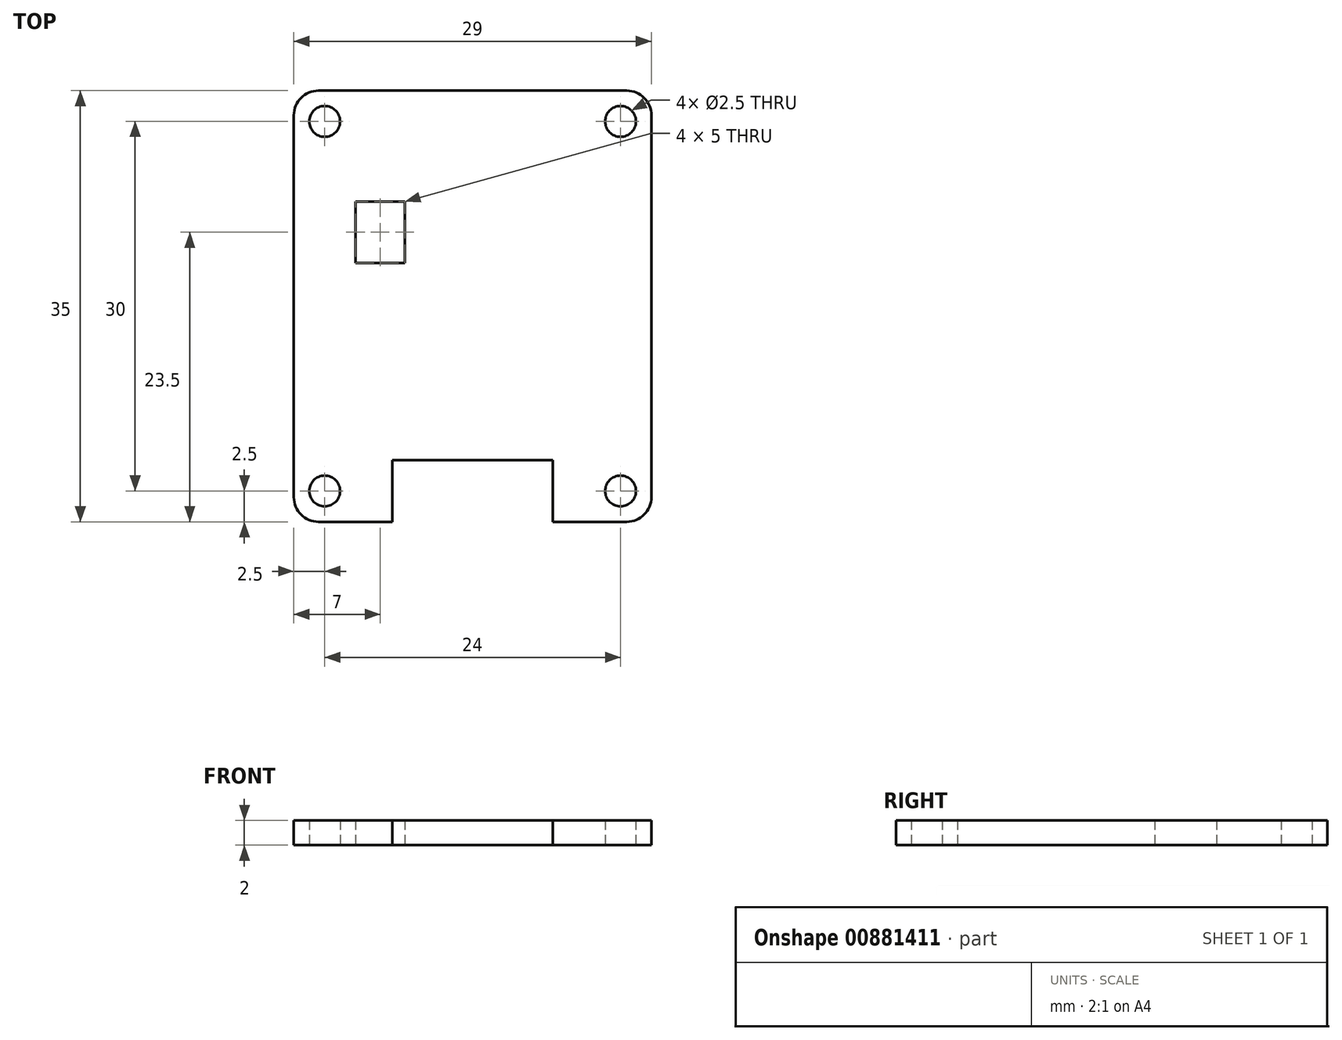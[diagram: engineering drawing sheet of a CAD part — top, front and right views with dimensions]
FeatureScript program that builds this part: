
annotation { "Feature Type Name" : "Feature", "Feature Type Description" : "" }
export const myFeature = defineFeature(function(context is Context, id is Id, definition is map)
    precondition{}
    {
        {
            var Q0;
            Q0=qCreatedBy(makeId("Top.planeOp"),FACE);
            var sketch = newSketch(context, id + "F0", { "sketchPlane" : qUnion([Q0])});
            skLineSegment(sketch, "E0.bottom", {"start": v(9.5, -12.5) * mm, "end": v(-9.5, -12.5) * mm});
            skLineSegment(sketch, "E0.top", {"start": v(9.5, 12.5) * mm, "end": v(-9.5, 12.5) * mm});
            skLineSegment(sketch, "E0.left", {"start": v(9.5, -12.5) * mm, "end": v(9.5, 12.5) * mm});
            skLineSegment(sketch, "E0.right", {"start": v(-9.5, -12.5) * mm, "end": v(-9.5, 12.5) * mm});
            skPoint(sketch, "E0.middle", {"position": v(0, 0) * mm});
            skLineSegment(sketch, "E1.0", {"start": v(14.5, 17.5) * mm, "end": v(-14.5, 17.5) * mm});
            skLineSegment(sketch, "E1.1", {"start": v(14.5, -17.5) * mm, "end": v(14.5, 17.5) * mm});
            skLineSegment(sketch, "E1.2", {"start": v(14.5, -17.5) * mm, "end": v(-14.5, -17.5) * mm});
            skLineSegment(sketch, "E1.3", {"start": v(-14.5, -17.5) * mm, "end": v(-14.5, 17.5) * mm});
            skPoint(sketch, "E2", {"position": v(12, 15) * mm});
            skPoint(sketch, "E3", {"position": v(-12, 15) * mm});
            skPoint(sketch, "E4", {"position": v(-12, -15) * mm});
            skPoint(sketch, "E5", {"position": v(12, -15) * mm});
            skCircle(sketch, "E6", {"center": v(-12, -15) * mm, "radius": 1.25 * mm});
            skCircle(sketch, "E7", {"center": v(12, -15) * mm, "radius": 1.25 * mm});
            skCircle(sketch, "E8", {"center": v(12, 15) * mm, "radius": 1.25 * mm});
            skCircle(sketch, "E9", {"center": v(-12, 15) * mm, "radius": 1.25 * mm});
            skPoint(sketch, "E10", {"position": v(-9.5, 8.5) * mm});
            skPoint(sketch, "E11", {"position": v(-5.5, 8.5) * mm});
            skPoint(sketch, "E12", {"position": v(-5.5, 3.5) * mm});
            skPoint(sketch, "E13", {"position": v(-9.5, 3.5) * mm});
            skLineSegment(sketch, "E14", {"start": v(-9.5, 8.5) * mm, "end": v(-5.5, 8.5) * mm});
            skLineSegment(sketch, "E15", {"start": v(-5.5, 8.5) * mm, "end": v(-5.5, 3.5) * mm});
            skLineSegment(sketch, "E16", {"start": v(-5.5, 3.5) * mm, "end": v(-9.5, 3.5) * mm});
            skPoint(sketch, "E17", {"position": v(6.5, -12.5) * mm});
            skPoint(sketch, "E18", {"position": v(-6.5, -12.5) * mm});
            skLineSegment(sketch, "E19", {"start": v(-6.5, -12.5) * mm, "end": v(-6.5, -17.5) * mm});
            skLineSegment(sketch, "E20", {"start": v(6.5, -12.5) * mm, "end": v(6.5, -17.5) * mm});
            skSolve(sketch);
        }
        {
            var Q0;
            Q0=makeQuery(id+"F0.imprint","IMPRINT",FACE,{"disambiguationData":[TD([[makeQuery(id+"F0.imprint","IMPRINT",EDGE,{"derivedFrom":sQuery(id+"F0.wireOp",EDGE,"E0.bottom")}),1.0]])]});
            var Q1;
            Q1=makeQuery(id+"F0.imprint","IMPRINT",FACE,{"disambiguationData":[TD([[makeQuery(id+"F0.imprint","IMPRINT",EDGE,{"derivedFrom":sQuery(id+"F0.wireOp",EDGE,"E0.bottom")}),-1.0]])]});
            extrude(context, id + "F1", {"entities" : qUnion([Q0, Q1]), "depth" : 2 * mm, "offsetDistance" : 25 * mm});
        }
        {
            var Q0;
            Q0=makeQuery(id+"F1.opExtrude","SWEPT_EDGE",EDGE,{"disambiguationData":[OSD([sQuery(id+"F0.wireOp",EDGE,"E1.0"),sQuery(id+"F0.wireOp",EDGE,"E1.3")])]});
            var Q1;
            Q1=makeQuery(id+"F1.opExtrude","SWEPT_EDGE",EDGE,{"disambiguationData":[OSD([sQuery(id+"F0.wireOp",EDGE,"E1.0"),sQuery(id+"F0.wireOp",EDGE,"E1.1")])]});
            var Q2;
            Q2=makeQuery(id+"F1.opExtrude","SWEPT_EDGE",EDGE,{"disambiguationData":[OSD([sQuery(id+"F0.wireOp",EDGE,"E1.1"),sQuery(id+"F0.wireOp",EDGE,"E1.2")])]});
            var Q3;
            Q3=makeQuery(id+"F1.opExtrude","SWEPT_EDGE",EDGE,{"disambiguationData":[OSD([sQuery(id+"F0.wireOp",EDGE,"E1.2"),sQuery(id+"F0.wireOp",EDGE,"E1.3")])]});
            fillet(context, id + "F2", {"entities" : qUnion([Q0, Q1, Q2, Q3]), "tangentPropagation" : true, "radius" : 2 * mm, "defaultsChanged" : false, "vertexSettings" : [], "allowEdgeOverflow" : false});
        }
    });
